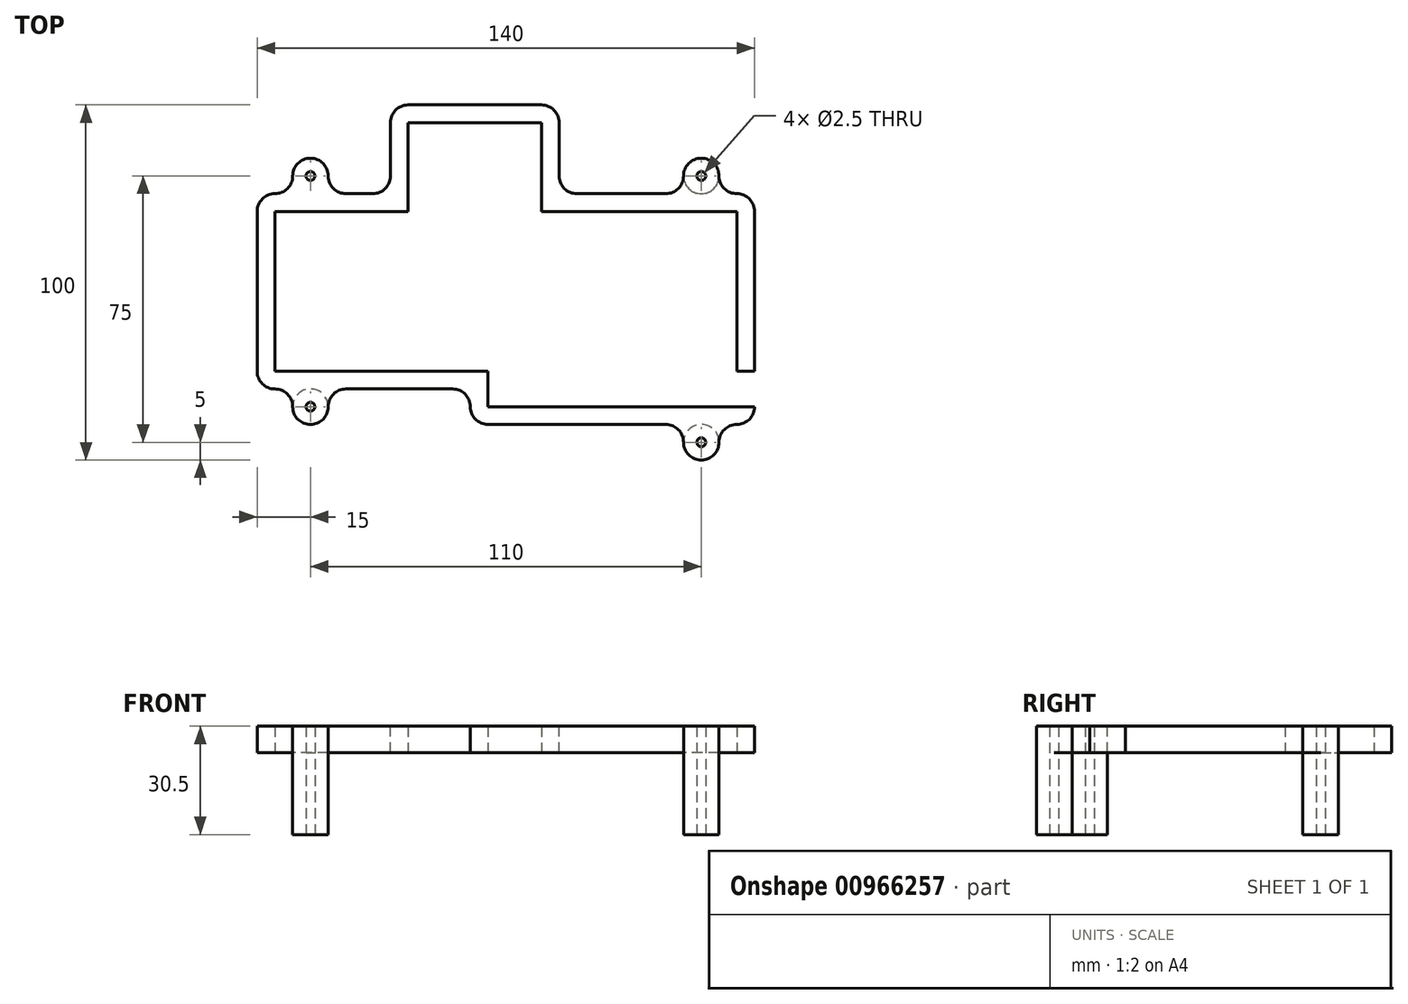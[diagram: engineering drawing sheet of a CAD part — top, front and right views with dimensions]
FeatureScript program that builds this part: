
annotation { "Feature Type Name" : "Feature", "Feature Type Description" : "" }
export const myFeature = defineFeature(function(context is Context, id is Id, definition is map)
    precondition{}
    {
        {
            var Q0;
            Q0=qCreatedBy(makeId("Top.planeOp"),FACE);
            var sketch = newSketch(context, id + "F0", { "sketchPlane" : qUnion([Q0])});
            skLineSegment(sketch, "E0.bottom", {"start": v(0, 0) * mm, "end": v(70, 0) * mm});
            skLineSegment(sketch, "E0.top", {"start": v(0, 55) * mm, "end": v(70, 55) * mm});
            skLineSegment(sketch, "E0.left", {"start": v(0, 0) * mm, "end": v(0, 55) * mm});
            skLineSegment(sketch, "E0.right", {"start": v(70, 0) * mm, "end": v(70, 55) * mm});
            skPoint(sketch, "E1", {"position": v(0, 27.5) * mm});
            skLineSegment(sketch, "E2.bottom", {"start": v(70, 55) * mm, "end": v(-60, 55) * mm});
            skLineSegment(sketch, "E2.top", {"start": v(70, 10) * mm, "end": v(-60, 10) * mm});
            skLineSegment(sketch, "E2.left", {"start": v(70, 55) * mm, "end": v(70, 10) * mm});
            skLineSegment(sketch, "E2.right", {"start": v(-60, 55) * mm, "end": v(-60, 10) * mm});
            skLineSegment(sketch, "E3.bottom", {"start": v(70, 55) * mm, "end": v(35, 55) * mm});
            skLineSegment(sketch, "E3.top", {"start": v(70, 0) * mm, "end": v(35, 0) * mm});
            skLineSegment(sketch, "E3.left", {"start": v(70, 55) * mm, "end": v(70, 0) * mm});
            skLineSegment(sketch, "E3.right", {"start": v(35, 55) * mm, "end": v(35, 0) * mm});
            skLineSegment(sketch, "E4.bottom", {"start": v(35, 55) * mm, "end": v(15, 55) * mm});
            skLineSegment(sketch, "E4.top", {"start": v(35, 0) * mm, "end": v(15, 0) * mm});
            skLineSegment(sketch, "E4.right", {"start": v(15, 55) * mm, "end": v(15, 0) * mm});
            skLineSegment(sketch, "E5.bottom", {"start": v(12.5, 52.5) * mm, "end": v(7.5, 52.5) * mm});
            skLineSegment(sketch, "E5.top", {"start": v(12.5, 40) * mm, "end": v(7.5, 40) * mm});
            skLineSegment(sketch, "E5.left", {"start": v(12.5, 52.5) * mm, "end": v(12.5, 40) * mm});
            skLineSegment(sketch, "E5.right", {"start": v(7.5, 52.5) * mm, "end": v(7.5, 40) * mm});
            skLineSegment(sketch, "E6.bottom", {"start": v(15, 55) * mm, "end": v(-22.5, 55) * mm});
            skLineSegment(sketch, "E6.top", {"start": v(15, 80) * mm, "end": v(-22.5, 80) * mm});
            skLineSegment(sketch, "E6.left", {"start": v(15, 55) * mm, "end": v(15, 80) * mm});
            skLineSegment(sketch, "E6.right", {"start": v(-22.5, 55) * mm, "end": v(-22.5, 80) * mm});
            skLineSegment(sketch, "E7.bottom", {"start": v(15, 40) * mm, "end": v(0, 40) * mm});
            skLineSegment(sketch, "E7.top", {"start": v(15, 80) * mm, "end": v(0, 80) * mm});
            skLineSegment(sketch, "E7.left", {"start": v(15, 40) * mm, "end": v(15, 80) * mm});
            skLineSegment(sketch, "E7.right", {"start": v(0, 40) * mm, "end": v(0, 80) * mm});
            skLineSegment(sketch, "E8.top", {"start": v(15, 10) * mm, "end": v(35, 10) * mm});
            skLineSegment(sketch, "E8.left", {"start": v(15, 5) * mm, "end": v(15, 10) * mm});
            skLineSegment(sketch, "E8.right", {"start": v(35, 5) * mm, "end": v(35, 10) * mm});
            skLineSegment(sketch, "E9.top", {"start": v(35, 55) * mm, "end": v(40, 55) * mm});
            skLineSegment(sketch, "E9.left", {"start": v(35, 5) * mm, "end": v(35, 55) * mm});
            skSolve(sketch);
        }
        {
            var Q0;
            Q0=qCreatedBy(makeId("Top.planeOp"),FACE);
            var sketch = newSketch(context, id + "F1", { "sketchPlane" : qUnion([Q0])});
            skLineSegment(sketch, "E10", {"start": v(75, 0) * mm, "end": v(75, 55) * mm});
            skLineSegment(sketch, "E11", {"start": v(20, 65) * mm, "end": v(20, 80) * mm});
            skLineSegment(sketch, "E12", {"start": v(15, 85) * mm, "end": v(-22.5, 85) * mm});
            skLineSegment(sketch, "E13", {"start": v(-27.5, 80) * mm, "end": v(-27.5, 65) * mm});
            skLineSegment(sketch, "E14", {"start": v(70, -5) * mm, "end": v(70, -5) * mm});
            skLineSegment(sketch, "E15", {"start": v(-5, 0) * mm, "end": v(-5, 0) * mm});
            skPoint(sketch, "E16.visualSharp", {"position": v(-65, 60) * mm});
            skArc(sketch, "E16.filletArc", {"start": v(-60, 60) * mm, "mid": v(-63.54, 58.54) * mm, "end": v(-65, 55) * mm});
            skPoint(sketch, "E17.visualSharp", {"position": v(-65, 5) * mm});
            skArc(sketch, "E17.filletArc", {"start": v(-65, 10) * mm, "mid": v(-63.54, 6.46) * mm, "end": v(-60, 5) * mm});
            skPoint(sketch, "E18.visualSharp", {"position": v(-5, -5) * mm});
            skArc(sketch, "E18.filletArc", {"start": v(-5, 0) * mm, "mid": v(-3.54, -3.54) * mm, "end": v(0, -5) * mm});
            skPoint(sketch, "E19.visualSharp", {"position": v(-5, 5) * mm});
            skArc(sketch, "E19.filletArc", {"start": v(-5, 0) * mm, "mid": v(-6.46, 3.54) * mm, "end": v(-10, 5) * mm});
            skPoint(sketch, "E20.visualSharp", {"position": v(75, -5) * mm});
            skArc(sketch, "E20.filletArc", {"start": v(70, -5) * mm, "mid": v(73.54, -3.54) * mm, "end": v(75, 0) * mm});
            skArc(sketch, "E21.filletArc", {"start": v(75, 55) * mm, "mid": v(73.54, 58.54) * mm, "end": v(70, 60) * mm});
            skPoint(sketch, "E22.visualSharp", {"position": v(20, 85) * mm});
            skArc(sketch, "E22.filletArc", {"start": v(20, 80) * mm, "mid": v(18.54, 83.54) * mm, "end": v(15, 85) * mm});
            skPoint(sketch, "E23.visualSharp", {"position": v(20, 60) * mm});
            skArc(sketch, "E23.filletArc", {"start": v(20, 65) * mm, "mid": v(21.46, 61.46) * mm, "end": v(25, 60) * mm});
            skPoint(sketch, "E24.visualSharp", {"position": v(-27.5, 85) * mm});
            skArc(sketch, "E24.filletArc", {"start": v(-22.5, 85) * mm, "mid": v(-26.04, 83.54) * mm, "end": v(-27.5, 80) * mm});
            skLineSegment(sketch, "E25.top", {"start": v(60, 70) * mm, "end": v(60, 70) * mm});
            skLineSegment(sketch, "E25.left", {"start": v(65, 65) * mm, "end": v(65, 65) * mm});
            skLineSegment(sketch, "E25.right", {"start": v(55, 65) * mm, "end": v(55, 65) * mm});
            skLineSegment(sketch, "E26", {"start": v(70, 60) * mm, "end": v(70, 60) * mm});
            skLineSegment(sketch, "E27", {"start": v(25, 60) * mm, "end": v(50, 60) * mm});
            skArc(sketch, "E28.filletArc", {"start": v(65, 65) * mm, "mid": v(66.46, 61.46) * mm, "end": v(70, 60) * mm});
            skArc(sketch, "E29.filletArc", {"start": v(50, 60) * mm, "mid": v(53.54, 61.46) * mm, "end": v(55, 65) * mm});
            skPoint(sketch, "E30.visualSharp", {"position": v(55, 70) * mm});
            skArc(sketch, "E30.filletArc", {"start": v(60, 70) * mm, "mid": v(56.46, 68.54) * mm, "end": v(55, 65) * mm});
            skPoint(sketch, "E31.visualSharp", {"position": v(65, 70) * mm});
            skArc(sketch, "E31.filletArc", {"start": v(65, 65) * mm, "mid": v(63.54, 68.54) * mm, "end": v(60, 70) * mm});
            skLineSegment(sketch, "E32.bottom", {"start": v(65, -5) * mm, "end": v(55, -5) * mm});
            skLineSegment(sketch, "E32.top", {"start": v(60, -15) * mm, "end": v(60, -15) * mm});
            skLineSegment(sketch, "E32.left", {"start": v(65, -10) * mm, "end": v(65, -10) * mm});
            skLineSegment(sketch, "E32.right", {"start": v(55, -10) * mm, "end": v(55, -10) * mm});
            skArc(sketch, "E33.filletArc", {"start": v(70, -5) * mm, "mid": v(66.46, -6.46) * mm, "end": v(65, -10) * mm});
            skLineSegment(sketch, "E34", {"start": v(50, -5) * mm, "end": v(0, -5) * mm});
            skPoint(sketch, "E35.visualSharp", {"position": v(55, -5) * mm});
            skArc(sketch, "E35.filletArc", {"start": v(55, -10) * mm, "mid": v(53.54, -6.46) * mm, "end": v(50, -5) * mm});
            skPoint(sketch, "E36.visualSharp", {"position": v(55, -15) * mm});
            skArc(sketch, "E36.filletArc", {"start": v(55, -10) * mm, "mid": v(56.46, -13.54) * mm, "end": v(60, -15) * mm});
            skPoint(sketch, "E37.visualSharp", {"position": v(65, -15) * mm});
            skArc(sketch, "E37.filletArc", {"start": v(60, -15) * mm, "mid": v(63.54, -13.54) * mm, "end": v(65, -10) * mm});
            skLineSegment(sketch, "E38.top", {"start": v(-50, 70) * mm, "end": v(-50, 70) * mm});
            skLineSegment(sketch, "E38.left", {"start": v(-55, 65) * mm, "end": v(-55, 65) * mm});
            skLineSegment(sketch, "E38.right", {"start": v(-45, 65) * mm, "end": v(-45, 65) * mm});
            skLineSegment(sketch, "E39", {"start": v(-40, 60) * mm, "end": v(-32.5, 60) * mm});
            skLineSegment(sketch, "E40", {"start": v(-60, 60) * mm, "end": v(-60, 60) * mm});
            skPoint(sketch, "E41.visualSharp", {"position": v(-27.5, 60) * mm});
            skArc(sketch, "E41.filletArc", {"start": v(-32.5, 60) * mm, "mid": v(-28.96, 61.46) * mm, "end": v(-27.5, 65) * mm});
            skArc(sketch, "E42.filletArc", {"start": v(-45, 65) * mm, "mid": v(-43.54, 61.46) * mm, "end": v(-40, 60) * mm});
            skPoint(sketch, "E43.visualSharp", {"position": v(-55, 60) * mm});
            skArc(sketch, "E43.filletArc", {"start": v(-60, 60) * mm, "mid": v(-56.46, 61.46) * mm, "end": v(-55, 65) * mm});
            skPoint(sketch, "E44.visualSharp", {"position": v(-45, 70) * mm});
            skArc(sketch, "E44.filletArc", {"start": v(-45, 65) * mm, "mid": v(-46.46, 68.54) * mm, "end": v(-50, 70) * mm});
            skPoint(sketch, "E45.visualSharp", {"position": v(-55, 70) * mm});
            skArc(sketch, "E45.filletArc", {"start": v(-50, 70) * mm, "mid": v(-53.54, 68.54) * mm, "end": v(-55, 65) * mm});
            skLineSegment(sketch, "E46.top", {"start": v(-50, -5) * mm, "end": v(-50, -5) * mm});
            skLineSegment(sketch, "E46.left", {"start": v(-55, 0) * mm, "end": v(-55, 0) * mm});
            skLineSegment(sketch, "E46.right", {"start": v(-45, 0) * mm, "end": v(-45, 0) * mm});
            skLineSegment(sketch, "E47", {"start": v(-60, 5) * mm, "end": v(-60, 5) * mm});
            skLineSegment(sketch, "E48", {"start": v(-40, 5) * mm, "end": v(-10, 5) * mm});
            skPoint(sketch, "E49.visualSharp", {"position": v(-55, 5) * mm});
            skArc(sketch, "E49.filletArc", {"start": v(-55, 0) * mm, "mid": v(-56.46, 3.54) * mm, "end": v(-60, 5) * mm});
            skPoint(sketch, "E50.visualSharp", {"position": v(-45, 5) * mm});
            skArc(sketch, "E50.filletArc", {"start": v(-40, 5) * mm, "mid": v(-43.54, 3.54) * mm, "end": v(-45, 0) * mm});
            skPoint(sketch, "E51.visualSharp", {"position": v(-45, -5) * mm});
            skArc(sketch, "E51.filletArc", {"start": v(-50, -5) * mm, "mid": v(-46.46, -3.54) * mm, "end": v(-45, 0) * mm});
            skPoint(sketch, "E52.visualSharp", {"position": v(-55, -5) * mm});
            skArc(sketch, "E52.filletArc", {"start": v(-55, 0) * mm, "mid": v(-53.54, -3.54) * mm, "end": v(-50, -5) * mm});
            skLineSegment(sketch, "E53", {"start": v(-22.5, 80) * mm, "end": v(-22.5, 55) * mm});
            skLineSegment(sketch, "E54", {"start": v(-22.5, 55) * mm, "end": v(-60, 55) * mm});
            skLineSegment(sketch, "E55", {"start": v(0, 10) * mm, "end": v(-60, 10) * mm});
            skLineSegment(sketch, "E56", {"start": v(0, 10) * mm, "end": v(0, 0) * mm});
            skLineSegment(sketch, "E57", {"start": v(0, 0) * mm, "end": v(70, 0) * mm});
            skLineSegment(sketch, "E58", {"start": v(70, 0) * mm, "end": v(70, 55) * mm});
            skLineSegment(sketch, "E59", {"start": v(70, 55) * mm, "end": v(15, 55) * mm});
            skLineSegment(sketch, "E60", {"start": v(15, 55) * mm, "end": v(15, 80) * mm});
            skLineSegment(sketch, "E61", {"start": v(-22.5, 80) * mm, "end": v(15, 80) * mm});
            skLineSegment(sketch, "E62", {"start": v(70, 10) * mm, "end": v(75, 10) * mm});
            skLineSegment(sketch, "E63", {"start": v(70, 0) * mm, "end": v(75, 0) * mm});
            skCircle(sketch, "E64", {"center": v(-50, 65) * mm, "radius": 5 * mm});
            skCircle(sketch, "E65", {"center": v(60, 65) * mm, "radius": 5 * mm});
            skCircle(sketch, "E66", {"center": v(60, -10) * mm, "radius": 5 * mm});
            skCircle(sketch, "E67", {"center": v(-50, 0) * mm, "radius": 5 * mm});
            skLineSegment(sketch, "E68.left", {"start": v(-60, 10) * mm, "end": v(-60, 55) * mm});
            skLineSegment(sketch, "E69", {"start": v(-65, 10) * mm, "end": v(-65, 55) * mm});
            skLineSegment(sketch, "E70.bottom", {"start": v(-65, 15) * mm, "end": v(-60, 15) * mm});
            skLineSegment(sketch, "E70.top", {"start": v(-65, 50) * mm, "end": v(-60, 50) * mm});
            skLineSegment(sketch, "E70.left", {"start": v(-65, 15) * mm, "end": v(-65, 50) * mm});
            skLineSegment(sketch, "E70.right", {"start": v(-60, 15) * mm, "end": v(-60, 50) * mm});
            skSolve(sketch);
        }
        {
            var Q0;
            Q0=makeQuery(id+"F1.imprint","IMPRINT",FACE,{"disambiguationData":[TD([[makeQuery(id+"F1.imprint","IMPRINT",EDGE,{"derivedFrom":sQuery(id+"F1.wireOp",EDGE,"E54")}),1.0]])]});
            var Q1;
            Q1=makeQuery(id+"F1.imprint","IMPRINT",FACE,{"disambiguationData":[TD([[makeQuery(id+"F1.imprint","IMPRINT",EDGE,{"derivedFrom":sQuery(id+"F1.wireOp",EDGE,"E11")}),1.0]])]});
            var Q2;
            {var subQ2=sQuery(id+"F1.wireOp",EDGE,"E62");Q2=makeQuery(id+"F1.imprint","IMPRINT",FACE,{"disambiguationData":[TD([[makeQuery(id+"F1.imprint","IMPRINT",EDGE,{"derivedFrom":subQ2}),-1.0]])]});}
            var Q3;
            {var subQ0=sQuery(id+"F1.wireOp",EDGE,"E64");var subQ1=makeQuery(id+"F1.imprint","INTERSECT",VERTEX,{"derivedFrom":[sQuery(id+"F1.wireOp",EDGE,"E42.filletArc"),subQ0]});Q3=makeQuery(id+"F1.imprint","IMPRINT",FACE,{"disambiguationData":[TD([[makeQuery(id+"F1.imprint","IMPRINT",EDGE,{"disambiguationData":[TD([[subQ1,-1.0]])],"derivedFrom":subQ0}),1.0]])]});}
            var Q4;
            {var subQ0=sQuery(id+"F1.wireOp",EDGE,"E65");var subQ1=makeQuery(id+"F1.imprint","INTERSECT",VERTEX,{"derivedFrom":[sQuery(id+"F1.wireOp",EDGE,"E28.filletArc"),subQ0]});Q4=makeQuery(id+"F1.imprint","IMPRINT",FACE,{"disambiguationData":[TD([[makeQuery(id+"F1.imprint","IMPRINT",EDGE,{"disambiguationData":[TD([[subQ1,-1.0]])],"derivedFrom":subQ0}),1.0]])]});}
            var Q5;
            {var subQ0=sQuery(id+"F1.wireOp",EDGE,"E66");var subQ2=makeQuery(id+"F1.imprint","IMPRINT",VERTEX,{"derivedFrom":subQ0});Q5=makeQuery(id+"F1.imprint","IMPRINT",FACE,{"disambiguationData":[TD([[makeQuery(id+"F1.imprint","IMPRINT",EDGE,{"disambiguationData":[TD([[subQ2,1.0]])],"derivedFrom":subQ0}),1.0]])]});}
            var Q6;
            {var subQ0=sQuery(id+"F1.wireOp",EDGE,"E67");var subQ1=makeQuery(id+"F1.imprint","INTERSECT",VERTEX,{"derivedFrom":[sQuery(id+"F1.wireOp",EDGE,"E49.filletArc"),subQ0]});Q6=makeQuery(id+"F1.imprint","IMPRINT",FACE,{"disambiguationData":[TD([[makeQuery(id+"F1.imprint","IMPRINT",EDGE,{"disambiguationData":[TD([[subQ1,1.0]])],"derivedFrom":subQ0}),1.0]])]});}
            var Q7;
            Q7=makeQuery(id+"F1.imprint","IMPRINT",FACE,{"disambiguationData":[TD([[makeQuery(id+"F1.imprint","IMPRINT",EDGE,{"derivedFrom":sQuery(id+"F1.wireOp",EDGE,"E70.bottom")}),1.0]])]});
            var Q8;
            {var subQ6=sQuery(id+"F1.wireOp",EDGE,"E17.filletArc");Q8=makeQuery(id+"F1.imprint","IMPRINT",FACE,{"disambiguationData":[TD([[makeQuery(id+"F1.imprint","IMPRINT",EDGE,{"derivedFrom":subQ6}),1.0]])]});}
            extrude(context, id + "F2", {"entities" : qUnion([Q0, Q1, Q2, Q3, Q4, Q5, Q6, Q7, Q8]), "oppositeDirection" : true, "depth" : 2.5 * mm, "offsetDistance" : 25 * mm});
        }
        {
            var Q0;
            Q0=makeQuery(id+"F1.imprint","IMPRINT",FACE,{"disambiguationData":[TD([[makeQuery(id+"F1.imprint","IMPRINT",EDGE,{"derivedFrom":sQuery(id+"F1.wireOp",EDGE,"E11")}),1.0]])]});
            var Q1;
            {var subQ0=sQuery(id+"F1.wireOp",EDGE,"E67");var subQ1=makeQuery(id+"F1.imprint","INTERSECT",VERTEX,{"derivedFrom":[sQuery(id+"F1.wireOp",EDGE,"E49.filletArc"),subQ0]});Q1=makeQuery(id+"F1.imprint","IMPRINT",FACE,{"disambiguationData":[TD([[makeQuery(id+"F1.imprint","IMPRINT",EDGE,{"disambiguationData":[TD([[subQ1,1.0]])],"derivedFrom":subQ0}),1.0]])]});}
            var Q2;
            {var subQ0=sQuery(id+"F1.wireOp",EDGE,"E66");var subQ2=makeQuery(id+"F1.imprint","IMPRINT",VERTEX,{"derivedFrom":subQ0});Q2=makeQuery(id+"F1.imprint","IMPRINT",FACE,{"disambiguationData":[TD([[makeQuery(id+"F1.imprint","IMPRINT",EDGE,{"disambiguationData":[TD([[subQ2,1.0]])],"derivedFrom":subQ0}),1.0]])]});}
            var Q3;
            {var subQ0=sQuery(id+"F1.wireOp",EDGE,"E65");var subQ1=makeQuery(id+"F1.imprint","INTERSECT",VERTEX,{"derivedFrom":[sQuery(id+"F1.wireOp",EDGE,"E28.filletArc"),subQ0]});Q3=makeQuery(id+"F1.imprint","IMPRINT",FACE,{"disambiguationData":[TD([[makeQuery(id+"F1.imprint","IMPRINT",EDGE,{"disambiguationData":[TD([[subQ1,-1.0]])],"derivedFrom":subQ0}),1.0]])]});}
            var Q4;
            {var subQ0=sQuery(id+"F1.wireOp",EDGE,"E64");var subQ1=makeQuery(id+"F1.imprint","INTERSECT",VERTEX,{"derivedFrom":[sQuery(id+"F1.wireOp",EDGE,"E42.filletArc"),subQ0]});Q4=makeQuery(id+"F1.imprint","IMPRINT",FACE,{"disambiguationData":[TD([[makeQuery(id+"F1.imprint","IMPRINT",EDGE,{"disambiguationData":[TD([[subQ1,-1.0]])],"derivedFrom":subQ0}),1.0]])]});}
            var Q5;
            {var subQ6=sQuery(id+"F1.wireOp",EDGE,"E17.filletArc");Q5=makeQuery(id+"F1.imprint","IMPRINT",FACE,{"disambiguationData":[TD([[makeQuery(id+"F1.imprint","IMPRINT",EDGE,{"derivedFrom":subQ6}),1.0]])]});}
            var Q6;
            Q6=makeQuery(id+"F1.imprint","IMPRINT",FACE,{"disambiguationData":[TD([[makeQuery(id+"F1.imprint","IMPRINT",EDGE,{"derivedFrom":sQuery(id+"F1.wireOp",EDGE,"E70.bottom")}),1.0]])]});
            extrude(context, id + "F3", {"entities" : qUnion([Q0, Q1, Q2, Q3, Q4, Q5, Q6]), "operationType" : NewBodyOperationType.ADD, "depth" : 28 * mm, "offsetDistance" : 25 * mm});
        }
        {
            var Q0;
            Q0=makeQuery(id+"F2.opExtrude","CAP_FACE",FACE,{"disambiguationData":[OSD([sQuery(id+"F1.wireOp",EDGE,"E10"),sQuery(id+"F1.wireOp",EDGE,"E11"),sQuery(id+"F1.wireOp",EDGE,"E12"),sQuery(id+"F1.wireOp",EDGE,"E13"),sQuery(id+"F1.wireOp",EDGE,"yh17EJ7i-H2ol-eNCa-Kbvx-fSuF8syH7sVV"),sQuery(id+"F1.wireOp",EDGE,"E16.filletArc"),sQuery(id+"F1.wireOp",EDGE,"E17.filletArc"),sQuery(id+"F1.wireOp",EDGE,"E18.filletArc"),sQuery(id+"F1.wireOp",EDGE,"E19.filletArc"),sQuery(id+"F1.wireOp",EDGE,"E20.filletArc"),sQuery(id+"F1.wireOp",EDGE,"E21.filletArc"),sQuery(id+"F1.wireOp",EDGE,"E22.filletArc"),sQuery(id+"F1.wireOp",EDGE,"E23.filletArc"),sQuery(id+"F1.wireOp",EDGE,"E24.filletArc"),sQuery(id+"F1.wireOp",EDGE,"E27"),sQuery(id+"F1.wireOp",EDGE,"E28.filletArc"),sQuery(id+"F1.wireOp",EDGE,"E29.filletArc"),sQuery(id+"F1.wireOp",EDGE,"E33.filletArc"),sQuery(id+"F1.wireOp",EDGE,"E34"),sQuery(id+"F1.wireOp",EDGE,"E35.filletArc"),sQuery(id+"F1.wireOp",EDGE,"E39"),sQuery(id+"F1.wireOp",EDGE,"E41.filletArc"),sQuery(id+"F1.wireOp",EDGE,"E42.filletArc"),sQuery(id+"F1.wireOp",EDGE,"E43.filletArc"),sQuery(id+"F1.wireOp",EDGE,"E48"),sQuery(id+"F1.wireOp",EDGE,"E49.filletArc"),sQuery(id+"F1.wireOp",EDGE,"E50.filletArc"),sQuery(id+"F1.wireOp",EDGE,"E64"),sQuery(id+"F1.wireOp",EDGE,"E65"),sQuery(id+"F1.wireOp",EDGE,"E66"),sQuery(id+"F1.wireOp",EDGE,"E67")])],"isStart":false});
            var sketch = newSketch(context, id + "F4", { "sketchPlane" : qUnion([Q0])});
            skCircle(sketch, "E71", {"center": v(-50, 0) * mm, "radius": 5 * mm});
            skCircle(sketch, "E72", {"center": v(60, 10) * mm, "radius": 5 * mm});
            skCircle(sketch, "E73", {"center": v(60, -65) * mm, "radius": 5 * mm});
            skCircle(sketch, "E74", {"center": v(-50, -65) * mm, "radius": 5 * mm});
            skSolve(sketch);
        }
        {
            var Q0;
            Q0=sQuery(id+"F4.wireOp",VERTEX,"E71.center");
            var Q1;
            Q1=sQuery(id+"F4.wireOp",VERTEX,"E72.center");
            var Q2;
            Q2=sQuery(id+"F4.wireOp",VERTEX,"E73.center");
            var Q3;
            Q3=sQuery(id+"F4.wireOp",VERTEX,"E74.center");
            var Q4;
            Q4=makeQuery(id+"F2.opExtrude","SWEPT_BODY",BODY,{"disambiguationData":[OSD([sQuery(id+"F1.wireOp",EDGE,"E10"),sQuery(id+"F1.wireOp",EDGE,"E11"),sQuery(id+"F1.wireOp",EDGE,"E12"),sQuery(id+"F1.wireOp",EDGE,"E13"),sQuery(id+"F1.wireOp",EDGE,"yh17EJ7i-H2ol-eNCa-Kbvx-fSuF8syH7sVV"),sQuery(id+"F1.wireOp",EDGE,"E16.filletArc"),sQuery(id+"F1.wireOp",EDGE,"E17.filletArc"),sQuery(id+"F1.wireOp",EDGE,"E18.filletArc"),sQuery(id+"F1.wireOp",EDGE,"E19.filletArc"),sQuery(id+"F1.wireOp",EDGE,"E20.filletArc"),sQuery(id+"F1.wireOp",EDGE,"E21.filletArc"),sQuery(id+"F1.wireOp",EDGE,"E22.filletArc"),sQuery(id+"F1.wireOp",EDGE,"E23.filletArc"),sQuery(id+"F1.wireOp",EDGE,"E24.filletArc"),sQuery(id+"F1.wireOp",EDGE,"E27"),sQuery(id+"F1.wireOp",EDGE,"E28.filletArc"),sQuery(id+"F1.wireOp",EDGE,"E29.filletArc"),sQuery(id+"F1.wireOp",EDGE,"E33.filletArc"),sQuery(id+"F1.wireOp",EDGE,"E34"),sQuery(id+"F1.wireOp",EDGE,"E35.filletArc"),sQuery(id+"F1.wireOp",EDGE,"E39"),sQuery(id+"F1.wireOp",EDGE,"E41.filletArc"),sQuery(id+"F1.wireOp",EDGE,"E42.filletArc"),sQuery(id+"F1.wireOp",EDGE,"E43.filletArc"),sQuery(id+"F1.wireOp",EDGE,"E48"),sQuery(id+"F1.wireOp",EDGE,"E49.filletArc"),sQuery(id+"F1.wireOp",EDGE,"E50.filletArc"),sQuery(id+"F1.wireOp",EDGE,"E64"),sQuery(id+"F1.wireOp",EDGE,"E65"),sQuery(id+"F1.wireOp",EDGE,"E66"),sQuery(id+"F1.wireOp",EDGE,"E67")])]});
            hole(context, id + "F5", {"style" : HoleStyle.SIMPLE, "endStyle" : HoleEndStyle.THROUGH, "holeDiameter" : 2.5 * mm, "majorDiameter" : 5 * mm, "isTappedThrough" : true, "tappedDepth" : 12 * mm, "tapClearance" : 3, "locations" : qUnion([Q0, Q1, Q2, Q3]), "scope" : qUnion([Q4])});
        }
        {
            var Q0;
            {var subQ2=sQuery(id+"F1.wireOp",EDGE,"E62");Q0=makeQuery(id+"F1.imprint","IMPRINT",FACE,{"disambiguationData":[TD([[makeQuery(id+"F1.imprint","IMPRINT",EDGE,{"derivedFrom":subQ2}),-1.0]])]});}
            extrude(context, id + "F6", {"entities" : qUnion([Q0]), "operationType" : NewBodyOperationType.ADD, "depth" : 20.5 * mm, "offsetDistance" : 25 * mm});
        }
        {
            var Q0;
            {var subQ5=sQuery(id+"F0.wireOp",EDGE,"E3.right");var subQ7=makeQuery(id+"F0.imprint","IMPRINT",VERTEX,{"derivedFrom":subQ5});Q0=makeQuery(id+"F0.imprint","IMPRINT",FACE,{"disambiguationData":[TD([[makeQuery(id+"F0.imprint","IMPRINT",EDGE,{"disambiguationData":[TD([[subQ7,-1.0]])],"derivedFrom":subQ5}),1.0]])]});}
            var Q1;
            {var subQ0=sQuery(id+"F0.wireOp",EDGE,"E3.right");var subQ3=makeQuery(id+"F0.imprint","IMPRINT",VERTEX,{"derivedFrom":subQ0});Q1=makeQuery(id+"F0.imprint","IMPRINT",FACE,{"disambiguationData":[TD([[makeQuery(id+"F0.imprint","IMPRINT",EDGE,{"disambiguationData":[TD([[subQ3,-1.0]])],"derivedFrom":subQ0}),-1.0]])]});}
            extrude(context, id + "F7", {"entities" : qUnion([Q0, Q1]), "operationType" : NewBodyOperationType.ADD, "depth" : 18 * mm, "offsetDistance" : 25 * mm});
        }
        {
            var Q0;
            Q0=makeQuery(id+"F1.imprint","IMPRINT",FACE,{"disambiguationData":[TD([[makeQuery(id+"F1.imprint","IMPRINT",EDGE,{"derivedFrom":sQuery(id+"F1.wireOp",EDGE,"E70.bottom")}),1.0]])]});
            extrude(context, id + "F8", {"entities" : qUnion([Q0]), "operationType" : NewBodyOperationType.REMOVE, "depth" : 10 * mm, "offsetDistance" : 25 * mm});
        }
        {
            var Q0;
            Q0=makeQuery(id+"F2.opExtrude","CAP_FACE",FACE,{"disambiguationData":[OSD([sQuery(id+"F1.wireOp",EDGE,"E10"),sQuery(id+"F1.wireOp",EDGE,"E11"),sQuery(id+"F1.wireOp",EDGE,"E12"),sQuery(id+"F1.wireOp",EDGE,"E13"),sQuery(id+"F1.wireOp",EDGE,"E16.filletArc"),sQuery(id+"F1.wireOp",EDGE,"E17.filletArc"),sQuery(id+"F1.wireOp",EDGE,"E18.filletArc"),sQuery(id+"F1.wireOp",EDGE,"E19.filletArc"),sQuery(id+"F1.wireOp",EDGE,"E20.filletArc"),sQuery(id+"F1.wireOp",EDGE,"E21.filletArc"),sQuery(id+"F1.wireOp",EDGE,"E22.filletArc"),sQuery(id+"F1.wireOp",EDGE,"E23.filletArc"),sQuery(id+"F1.wireOp",EDGE,"E24.filletArc"),sQuery(id+"F1.wireOp",EDGE,"E27"),sQuery(id+"F1.wireOp",EDGE,"E28.filletArc"),sQuery(id+"F1.wireOp",EDGE,"E29.filletArc"),sQuery(id+"F1.wireOp",EDGE,"E33.filletArc"),sQuery(id+"F1.wireOp",EDGE,"E34"),sQuery(id+"F1.wireOp",EDGE,"E35.filletArc"),sQuery(id+"F1.wireOp",EDGE,"E39"),sQuery(id+"F1.wireOp",EDGE,"E41.filletArc"),sQuery(id+"F1.wireOp",EDGE,"E42.filletArc"),sQuery(id+"F1.wireOp",EDGE,"E43.filletArc"),sQuery(id+"F1.wireOp",EDGE,"E48"),sQuery(id+"F1.wireOp",EDGE,"E49.filletArc"),sQuery(id+"F1.wireOp",EDGE,"E50.filletArc"),sQuery(id+"F1.wireOp",EDGE,"E64"),sQuery(id+"F1.wireOp",EDGE,"E65"),sQuery(id+"F1.wireOp",EDGE,"E66"),sQuery(id+"F1.wireOp",EDGE,"E67"),sQuery(id+"F1.wireOp",EDGE,"E69"),sQuery(id+"F1.wireOp",EDGE,"E70.left")])],"isStart":false});
            var sketch = newSketch(context, id + "F9", { "sketchPlane" : qUnion([Q0])});
            skCircle(sketch, "E75", {"center": v(-50, 0) * mm, "radius": 5 * mm});
            skCircle(sketch, "E76", {"center": v(60, 10) * mm, "radius": 5 * mm});
            skCircle(sketch, "E77", {"center": v(60, -65) * mm, "radius": 5 * mm});
            skCircle(sketch, "E78", {"center": v(-50, -65) * mm, "radius": 5 * mm});
            skSolve(sketch);
        }
        {
            var Q0;
            {var subQ0=sQuery(id+"F9.wireOp",EDGE,"E75");Q0=makeQuery(id+"F9.imprint","IMPRINT",FACE,{"disambiguationData":[TD([[makeQuery(id+"F9.imprint","IMPRINT",EDGE,{"disambiguationData":[OD(0.0)],"derivedFrom":subQ0}),-1.0]])]});}
            var Q1;
            {var subQ0=sQuery(id+"F9.wireOp",EDGE,"E76");Q1=makeQuery(id+"F9.imprint","IMPRINT",FACE,{"disambiguationData":[TD([[makeQuery(id+"F9.imprint","IMPRINT",EDGE,{"disambiguationData":[OD(0.0)],"derivedFrom":subQ0}),-1.0]])]});}
            var Q2;
            {var subQ0=sQuery(id+"F9.wireOp",EDGE,"E77");Q2=makeQuery(id+"F9.imprint","IMPRINT",FACE,{"disambiguationData":[TD([[makeQuery(id+"F9.imprint","IMPRINT",EDGE,{"disambiguationData":[OD(0.0)],"derivedFrom":subQ0}),1.0]])]});}
            var Q3;
            {var subQ0=sQuery(id+"F9.wireOp",EDGE,"E78");Q3=makeQuery(id+"F9.imprint","IMPRINT",FACE,{"disambiguationData":[TD([[makeQuery(id+"F9.imprint","IMPRINT",EDGE,{"disambiguationData":[OD(0.0)],"derivedFrom":subQ0}),-1.0]])]});}
            extrude(context, id + "F10", {"entities" : qUnion([Q0, Q1, Q2, Q3]), "operationType" : NewBodyOperationType.REMOVE, "oppositeDirection" : true, "depth" : 23 * mm, "offsetDistance" : 25 * mm});
        }
    });
